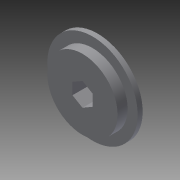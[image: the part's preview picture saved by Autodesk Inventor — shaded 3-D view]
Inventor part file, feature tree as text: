
AUTODESK INVENTOR PART (.ipt)
format: ipt  version: 2014 (Build 180170000, 170)  size: 98,304 bytes
history: native  units: in
note: dims shown in document units (in); Inventor stores cm internally (conversion verified against a paired STEP export)
features: extrude x2, sketch x2
ambient origin geometry x8: Origin, YZ Plane, XZ Plane, XY Plane, X Axis, Y Axis, Z Axis, Center Point
bodies: Solid1 (feature_tree)
feature tree (4):
  extrude  "Extrusion1"  Depth=0.5in
  extrude  "Extrusion3"  Depth=0.25in
  sketch  "Sketch1"  dims[d0=2.25in d1=0.5in]
  sketch  "Sketch3"  dims[d2=0.125in d3=0.0in d8=1.75in d9=0.25in d10=0.0in]
